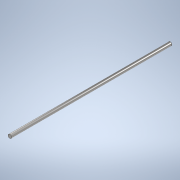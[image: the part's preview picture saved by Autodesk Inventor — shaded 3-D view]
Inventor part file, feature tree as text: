
AUTODESK INVENTOR PART (.ipt)
format: ipt  version: 2020 (Build 240168000, 168)  size: 93,184 bytes
history: native  units: in
note: dims shown in document units (in); Inventor stores cm internally (conversion verified against a paired STEP export)
features: extrude x1, sketch x1
ambient origin geometry x8: Origin, YZ Plane, XZ Plane, XY Plane, X Axis, Y Axis, Z Axis, Center Point
bodies: Solid1 (feature_tree)
feature tree (2):
  extrude  "Extrusion1"  Depth=7.0in TaperAngle=0.0deg
  sketch  "Sketch1"  dims[d0=0.1575in d1=7.0in d2=0.0in]
